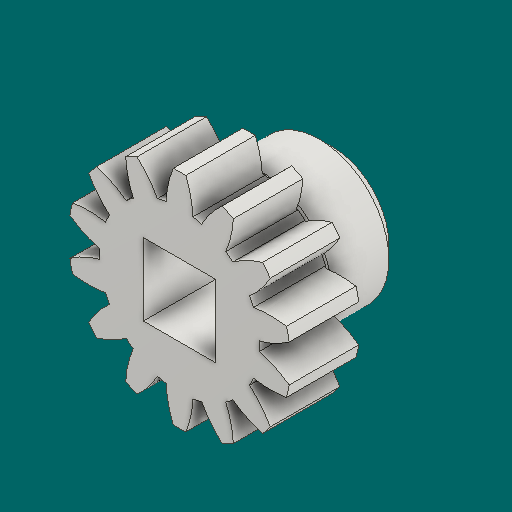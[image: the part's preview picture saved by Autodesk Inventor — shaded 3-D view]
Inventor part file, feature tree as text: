
AUTODESK INVENTOR PART (.ipt)
format: ipt  version: 2023.1 (Build 271208000, 208)  size: 322,560 bytes
history: native  units: in
note: dims shown in document units (in); Inventor stores cm internally (conversion verified against a paired STEP export)
features: other x12, sketch x5, plane x4
ambient origin geometry x8: Origin, YZ Plane, XZ Plane, XY Plane, X Axis, Y Axis, Z Axis, Center Point
bodies: Solid1 (feature_tree)
feature tree (21):
  other  "Spur Gear1"
  other  "Solid1::Spur Gear1"
  other  "TaggingFeature1"
  sketch  "Sketch1"  dims[d0=0.3937in]
  sketch  "Sketch2"  dims[d9=0.0in]
  sketch  "Sketch3"  dims[d14=0.0in]
  sketch  "Sketch4"  dims[d15=0.7in]
  sketch  "Sketch5"  dims[d16=0.0in d17=0.0in d18=0.0in d19=0.7in]
  plane  "XZ Plane_1"
  plane  "Work Plane2"
  plane  "Work Plane3"
  plane  "Work Plane4"
  other  "Srf1"
  other  "Srf1::Derived"
  other  "Start plane iMate"
  other  "Distance iMate"
  other  "Position iMate"
  other  "Mesh iMate"
  other  "Axis iMate"
  other  "Mesh iMate2"
  other  "Align iMate"
